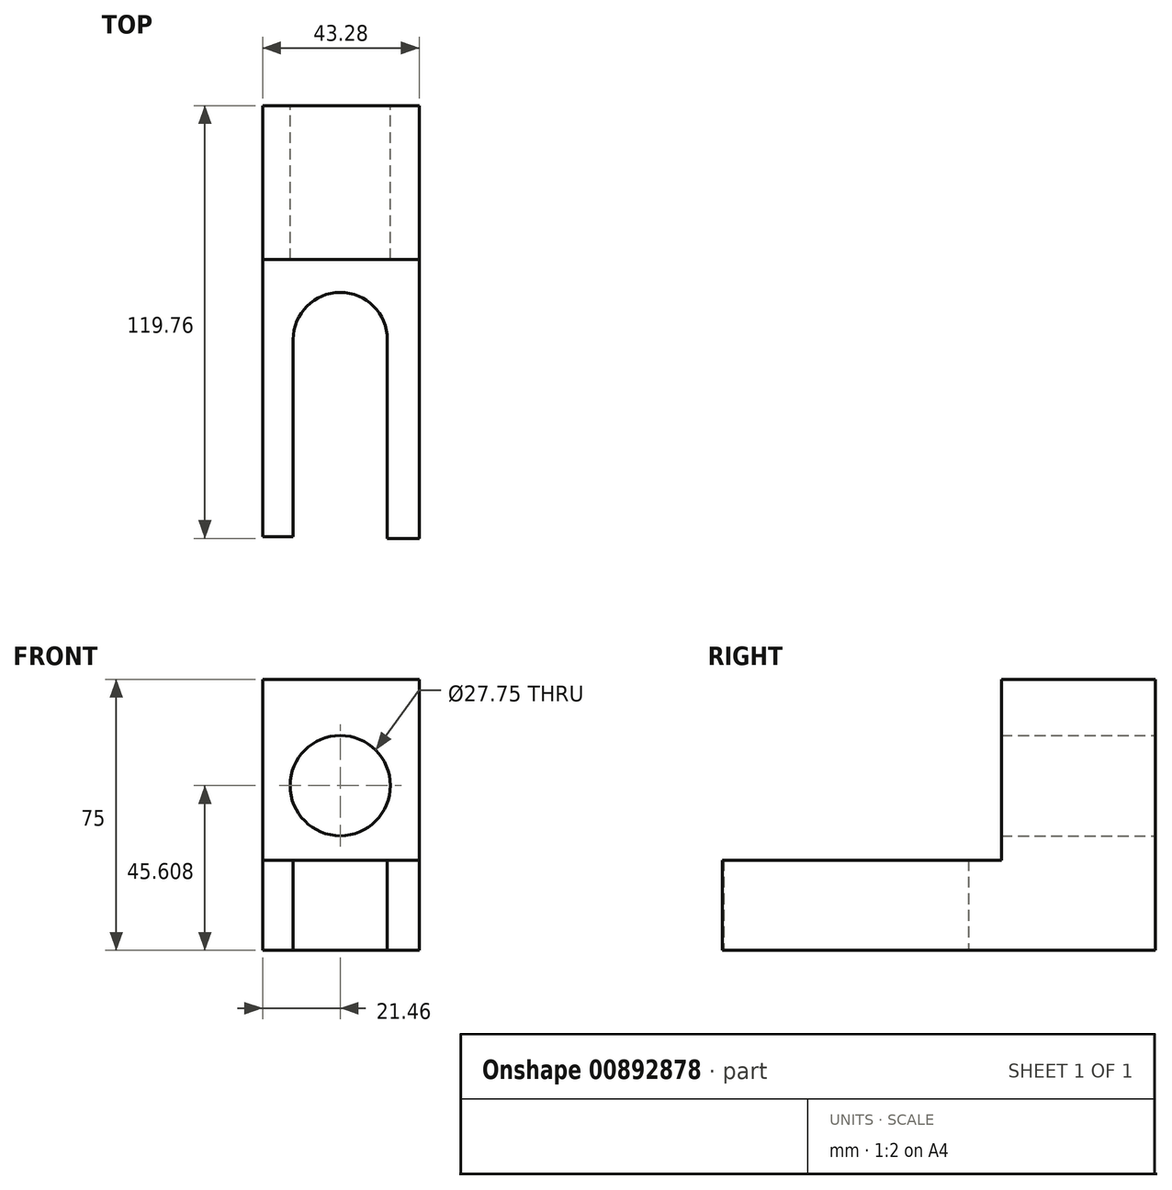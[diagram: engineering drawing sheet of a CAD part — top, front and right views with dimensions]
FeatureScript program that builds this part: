
annotation { "Feature Type Name" : "Feature", "Feature Type Description" : "" }
export const myFeature = defineFeature(function(context is Context, id is Id, definition is map)
    precondition{}
    {
        {
            var Q0;
            Q0=qCreatedBy(makeId("Top.planeOp"),FACE);
            var sketch = newSketch(context, id + "F0", { "sketchPlane" : qUnion([Q0])});
            skCircle(sketch, "E0", {"center": v(0, 0) * mm, "radius": 13 * mm});
            skCircle(sketch, "E1", {"center": v(0, 0) * mm, "radius": 21.46 * mm});
            skLineSegment(sketch, "E2", {"start": v(-21.46, 0) * mm, "end": v(-21.46, 64.7) * mm});
            skLineSegment(sketch, "E3", {"start": v(-21.46, 64.7) * mm, "end": v(21.82, 64.7) * mm});
            skLineSegment(sketch, "E4", {"start": v(21.82, 64.7) * mm, "end": v(21.82, 0) * mm});
            skLineSegment(sketch, "E5", {"start": v(21.82, 0) * mm, "end": v(21.82, -55.05) * mm});
            skLineSegment(sketch, "E6", {"start": v(21.82, -55.05) * mm, "end": v(13, -55.05) * mm});
            skLineSegment(sketch, "E7", {"start": v(13, -55.05) * mm, "end": v(13, 0) * mm});
            skLineSegment(sketch, "E8", {"start": v(-21.46, 0) * mm, "end": v(-21.46, -54.63) * mm});
            skLineSegment(sketch, "E9", {"start": v(-21.46, -54.63) * mm, "end": v(-13, -54.63) * mm});
            skLineSegment(sketch, "E10", {"start": v(-13, -54.63) * mm, "end": v(-13, 0) * mm});
            skSolve(sketch);
        }
        {
            var Q0;
            {var subQ0=sQuery(id+"F0.wireOp",EDGE,"E2");Q0=makeQuery(id+"F0.imprint","IMPRINT",FACE,{"disambiguationData":[TD([[makeQuery(id+"F0.imprint","IMPRINT",EDGE,{"derivedFrom":subQ0}),-1.0]])]});}
            var Q1;
            {var subQ0=sQuery(id+"F0.wireOp",EDGE,"E8");Q1=makeQuery(id+"F0.imprint","IMPRINT",FACE,{"disambiguationData":[TD([[makeQuery(id+"F0.imprint","IMPRINT",EDGE,{"derivedFrom":subQ0}),1.0]])]});}
            var Q2;
            {var subQ0=sQuery(id+"F0.wireOp",EDGE,"E7");var subQ1=sQuery(id+"F0.wireOp",EDGE,"E0");var subQ2=makeQuery(id+"F0.imprint","INTERSECT",VERTEX,{"derivedFrom":[subQ1,subQ0]});Q2=makeQuery(id+"F0.imprint","IMPRINT",FACE,{"disambiguationData":[TD([[makeQuery(id+"F0.imprint","IMPRINT",EDGE,{"disambiguationData":[TD([[subQ2,-1.0]])],"derivedFrom":subQ1}),-1.0]])]});}
            extrude(context, id + "F1", {"entities" : qUnion([Q0, Q1, Q2]), "depth" : 25 * mm, "offsetDistance" : 25 * mm});
        }
        {
            var Q0;
            Q0=makeQuery(id+"F1.opExtrude","CAP_FACE",FACE,{"disambiguationData":[OSD([sQuery(id+"F0.wireOp",EDGE,"E0"),sQuery(id+"F0.wireOp",EDGE,"E2"),sQuery(id+"F0.wireOp",EDGE,"E3"),sQuery(id+"F0.wireOp",EDGE,"E4"),sQuery(id+"F0.wireOp",EDGE,"E5"),sQuery(id+"F0.wireOp",EDGE,"E6"),sQuery(id+"F0.wireOp",EDGE,"E7"),sQuery(id+"F0.wireOp",EDGE,"E8"),sQuery(id+"F0.wireOp",EDGE,"E9"),sQuery(id+"F0.wireOp",EDGE,"E10")])],"isStart":false});
            var sketch = newSketch(context, id + "F2", { "sketchPlane" : qUnion([Q0])});
            skLineSegment(sketch, "E11", {"start": v(21.82, 22.16) * mm, "end": v(-21.46, 22.16) * mm});
            skSolve(sketch);
        }
        {
            var Q0;
            {var subQ0=sQuery(id+"F2.wireOp",EDGE,"E11");Q0=makeQuery(id+"F2.imprint","IMPRINT",FACE,{"disambiguationData":[TD([[makeQuery(id+"F2.imprint","IMPRINT",EDGE,{"derivedFrom":subQ0}),-1.0]])]});}
            extrude(context, id + "F3", {"entities" : qUnion([Q0]), "operationType" : NewBodyOperationType.ADD, "depth" : 50 * mm, "offsetDistance" : 25 * mm});
        }
        {
            var Q0;
            {var subQ0=sQuery(id+"F0.wireOp",EDGE,"E3");Q0=makeQuery(id+"F3.boolean.opBoolean","MERGE",FACE,{"derivedFrom":[makeQuery(id+"F1.opExtrude","SWEPT_FACE",FACE,{"disambiguationData":[OSD([subQ0])]}),makeQuery(id+"F3.opExtrude","SWEPT_FACE",FACE,{"disambiguationData":[OSD([subQ0])]})]});}
            var sketch = newSketch(context, id + "F4", { "sketchPlane" : qUnion([Q0])});
            skCircle(sketch, "E12", {"center": v(0, 45.6) * mm, "radius": 13.88 * mm});
            skSolve(sketch);
        }
        {
            var Q0;
            Q0=makeQuery(id+"F4.imprint","IMPRINT",FACE,{"disambiguationData":[TD([[makeQuery(id+"F4.imprint","IMPRINT",EDGE,{"derivedFrom":sQuery(id+"F4.wireOp",EDGE,"E12")}),1.0]])]});
            var Q1;
            Q1=sQuery(id+"F4.wireOp",EDGE,"E12");
            extrude(context, id + "F5", {"entities" : qUnion([Q0]), "operationType" : NewBodyOperationType.REMOVE, "surfaceEntities" : qUnion([Q1]), "endBound" : BoundingType.THROUGH_ALL, "oppositeDirection" : true, "depth" : 25 * mm, "offsetDistance" : 25 * mm});
        }
    });
